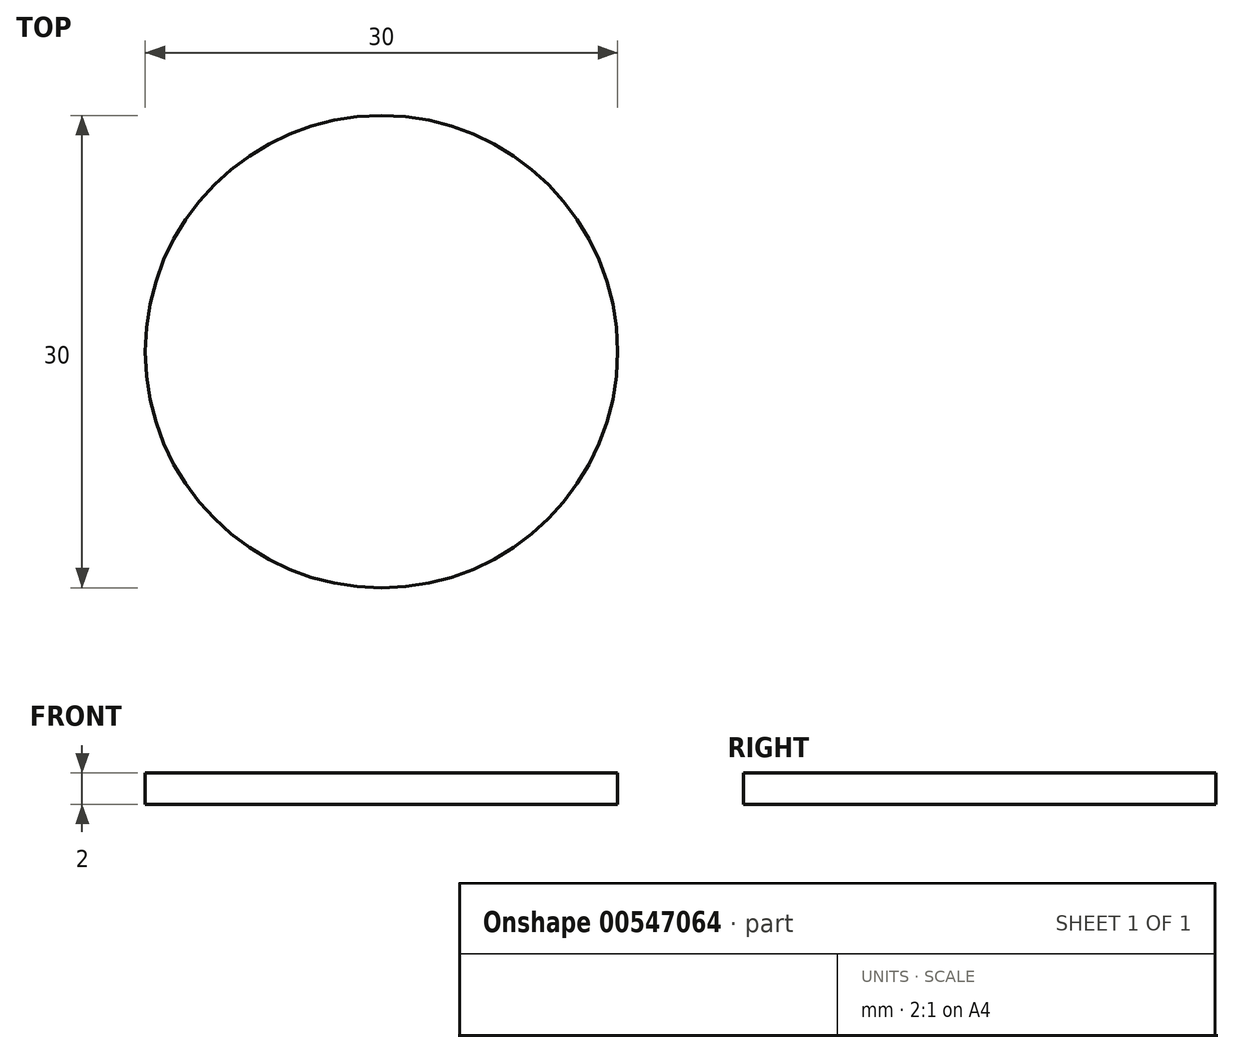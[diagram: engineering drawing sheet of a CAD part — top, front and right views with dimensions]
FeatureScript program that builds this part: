
annotation { "Feature Type Name" : "Feature", "Feature Type Description" : "" }
export const myFeature = defineFeature(function(context is Context, id is Id, definition is map)
    precondition{}
    {
        {
            var Q0;
            Q0=qCreatedBy(makeId("Top.planeOp"),FACE);
            var sketch = newSketch(context, id + "F0", { "sketchPlane" : qUnion([Q0])});
            skCircle(sketch, "E0", {"center": v(0, 0) * mm, "radius": 15 * mm});
            skSolve(sketch);
        }
        {
            var Q0;
            Q0=makeQuery(id+"F0.imprint","IMPRINT",FACE,{"disambiguationData":[TD([[makeQuery(id+"F0.imprint","IMPRINT",EDGE,{"derivedFrom":sQuery(id+"F0.wireOp",EDGE,"E0")}),1.0]])]});
            extrude(context, id + "F1", {"entities" : qUnion([Q0]), "depth" : 2 * mm, "offsetDistance" : 25 * mm});
        }
    });
